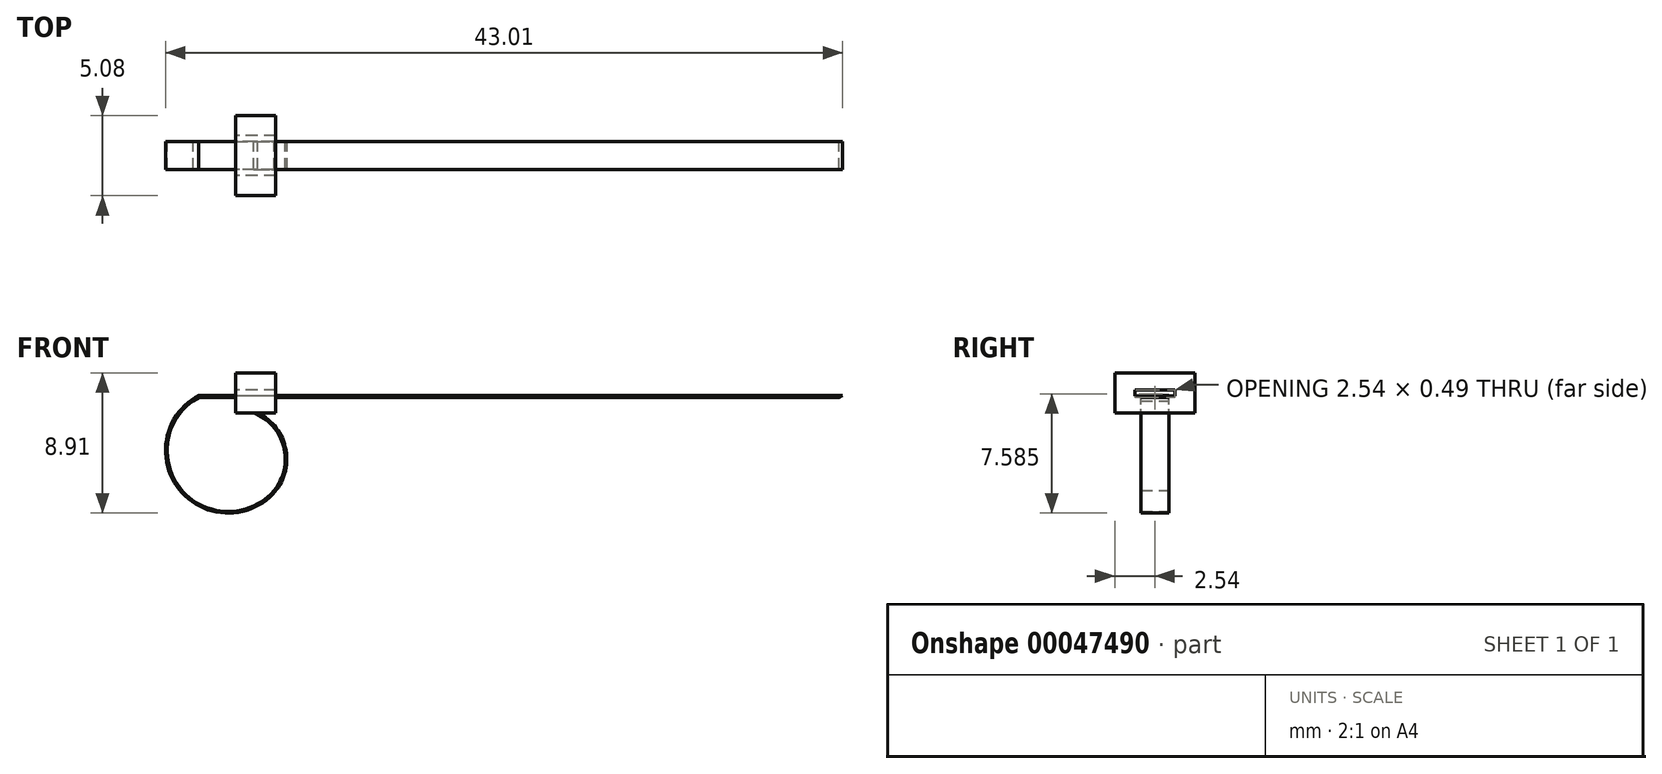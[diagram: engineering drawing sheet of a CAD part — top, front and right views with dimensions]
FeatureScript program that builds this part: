
annotation { "Feature Type Name" : "Feature", "Feature Type Description" : "" }
export const myFeature = defineFeature(function(context is Context, id is Id, definition is map)
    precondition{}
    {
        {
            var Q0;
            Q0=qCreatedBy(makeId("Right.planeOp"),FACE);
            var sketch = newSketch(context, id + "F0", { "sketchPlane" : qUnion([Q0])});
            skLineSegment(sketch, "E0.rect.bottom", {"start": v(-2.54, 1.27) * mm, "end": v(2.54, 1.27) * mm});
            skLineSegment(sketch, "E0.rect.top", {"start": v(-2.54, -1.27) * mm, "end": v(2.54, -1.27) * mm});
            skLineSegment(sketch, "E0.rect.left", {"start": v(-2.54, 1.27) * mm, "end": v(-2.54, -1.27) * mm});
            skLineSegment(sketch, "E0.rect.right", {"start": v(2.54, 1.27) * mm, "end": v(2.54, -1.27) * mm});
            skPoint(sketch, "E0.rect.middle", {"position": v(0, 0) * mm});
            skSolve(sketch);
        }
        {
            var Q0;
            Q0 = qSketchRegion(id + "F0", true);
            extrude(context, id + "F1", {"entities" : qUnion([Q0]), "depth" : 2.54 * mm, "symmetric" : true});
        }
        {
            var Q0;
            Q0=qCreatedBy(makeId("Front.planeOp"),FACE);
            var sketch = newSketch(context, id + "F2", { "sketchPlane" : qUnion([Q0])});
            skArc(sketch, "E1", {"start": v(0.98, -6.77) * mm, "mid": v(2.09, -3.63) * mm, "end": v(0, -1.04) * mm});
            skArc(sketch, "E2", {"start": v(0.98, -6.77) * mm, "mid": v(-5.16, -6) * mm, "end": v(-3.67, 0) * mm});
            skLineSegment(sketch, "E3", {"start": v(-3.67, 0) * mm, "end": v(37.57, 0) * mm});
            skSolve(sketch);
        }
        {
            var Q0;
            Q0=makeQuery(id+"F1.opExtrude","CAP_FACE",FACE,{"disambiguationData":[OSD([sQuery(id+"F0.wireOp",EDGE,"E0.rect.bottom"),sQuery(id+"F0.wireOp",EDGE,"E0.rect.top"),sQuery(id+"F0.wireOp",EDGE,"E0.rect.left"),sQuery(id+"F0.wireOp",EDGE,"E0.rect.right")])],"isStart":true});
            var sketch = newSketch(context, id + "F3", { "sketchPlane" : qUnion([Q0])});
            skLineSegment(sketch, "E4.rect.bottom", {"start": v(-1.27, 0.2) * mm, "end": v(1.27, 0.2) * mm});
            skLineSegment(sketch, "E4.rect.top", {"start": v(-1.27, -0.2) * mm, "end": v(1.27, -0.2) * mm});
            skLineSegment(sketch, "E4.rect.left", {"start": v(-1.27, 0.2) * mm, "end": v(-1.27, -0.2) * mm});
            skLineSegment(sketch, "E4.rect.right", {"start": v(1.27, 0.2) * mm, "end": v(1.27, -0.2) * mm});
            skPoint(sketch, "E4.rect.middle", {"position": v(0, 0) * mm});
            skSolve(sketch);
        }
        {
            var Q0;
            Q0 = qSketchRegion(id + "F3", true);
            var Q1;
            Q1=makeQuery(id+"F1.opExtrude","CAP_FACE",FACE,{"disambiguationData":[OSD([sQuery(id+"F0.wireOp",EDGE,"E0.rect.bottom"),sQuery(id+"F0.wireOp",EDGE,"E0.rect.top"),sQuery(id+"F0.wireOp",EDGE,"E0.rect.left"),sQuery(id+"F0.wireOp",EDGE,"E0.rect.right")])],"isStart":false});
            extrude(context, id + "F4", {"entities" : qUnion([Q0]), "operationType" : NewBodyOperationType.REMOVE, "endBound" : BoundingType.UP_TO_SURFACE, "oppositeDirection" : true, "endBoundEntityFace" : qUnion([Q1]), "depth" : 25.4 * mm});
        }
        {
            var Q0;
            Q0=makeQuery(id+"F1.opExtrude","SWEPT_FACE",FACE,{"disambiguationData":[OSD([sQuery(id+"F0.wireOp",EDGE,"E0.rect.top")])]});
            var sketch = newSketch(context, id + "F5", { "sketchPlane" : qUnion([Q0])});
            skLineSegment(sketch, "E5.rect.bottom", {"start": v(-0.13, 0.89) * mm, "end": v(0.13, 0.89) * mm});
            skLineSegment(sketch, "E5.rect.top", {"start": v(-0.13, -0.89) * mm, "end": v(0.13, -0.89) * mm});
            skLineSegment(sketch, "E5.rect.left", {"start": v(-0.13, 0.89) * mm, "end": v(-0.13, -0.89) * mm});
            skLineSegment(sketch, "E5.rect.right", {"start": v(0.13, 0.89) * mm, "end": v(0.13, -0.89) * mm});
            skPoint(sketch, "E5.rect.middle", {"position": v(0, 0) * mm});
            skSolve(sketch);
        }
        {
            var Q0;
            Q0 = qSketchRegion(id + "F5", true);
            var Q1;
            Q1 = qConstructionFilter(qBodyType(qCreatedBy(id + "F2" ,EDGE), BodyType.WIRE), ConstructionObject.NO);
            sweep(context, id + "F6", {"operationType" : NewBodyOperationType.ADD, "profiles" : qUnion([Q0]), "path" : qUnion([Q1])});
        }
    });
